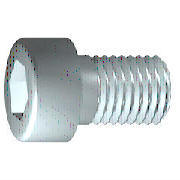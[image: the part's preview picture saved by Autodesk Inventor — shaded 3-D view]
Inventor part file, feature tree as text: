
AUTODESK INVENTOR PART (.ipt)
format: ipt  version: 2013 (Build 170138000, 138)  size: 191,488 bytes
history: native  units: mm (DEFAULTED — no unit token found)
features: sketch x2, extrude x1, plane x1, fillet x1
ambient origin geometry x7: Origin, YZ Plane, XY Plane, X Axis, Y Axis, Z Axis, Center Point
bodies: Solid1 (feature_tree), Body (feature_tree)
feature tree (5):
  extrude  "Slot"  Depth=0.306825mm
  plane  "Work Plane1"
  fillet  "Fillet2"  Radius=3.0mm
  sketch  "Sketch1"  dims[d1=6.693275mm d2=0.306825mm d3=3.0mm]
  sketch  "Sketch2"  dims[d4=1.5mm d5=60.0deg d6=3.0mm d7=3.0mm d8=2.886751mm d9=5.5mm d10=90.0deg d11=10.0mm d12=0.0mm d13=6.693275mm d14=0.0mm d15=0.306725mm d16=0.306725mm d17=0.3mm d19=0.0mm d26=8.0mm d27=45.0deg d28=0.0mm d29=0.0mm d30=0.1mm]
